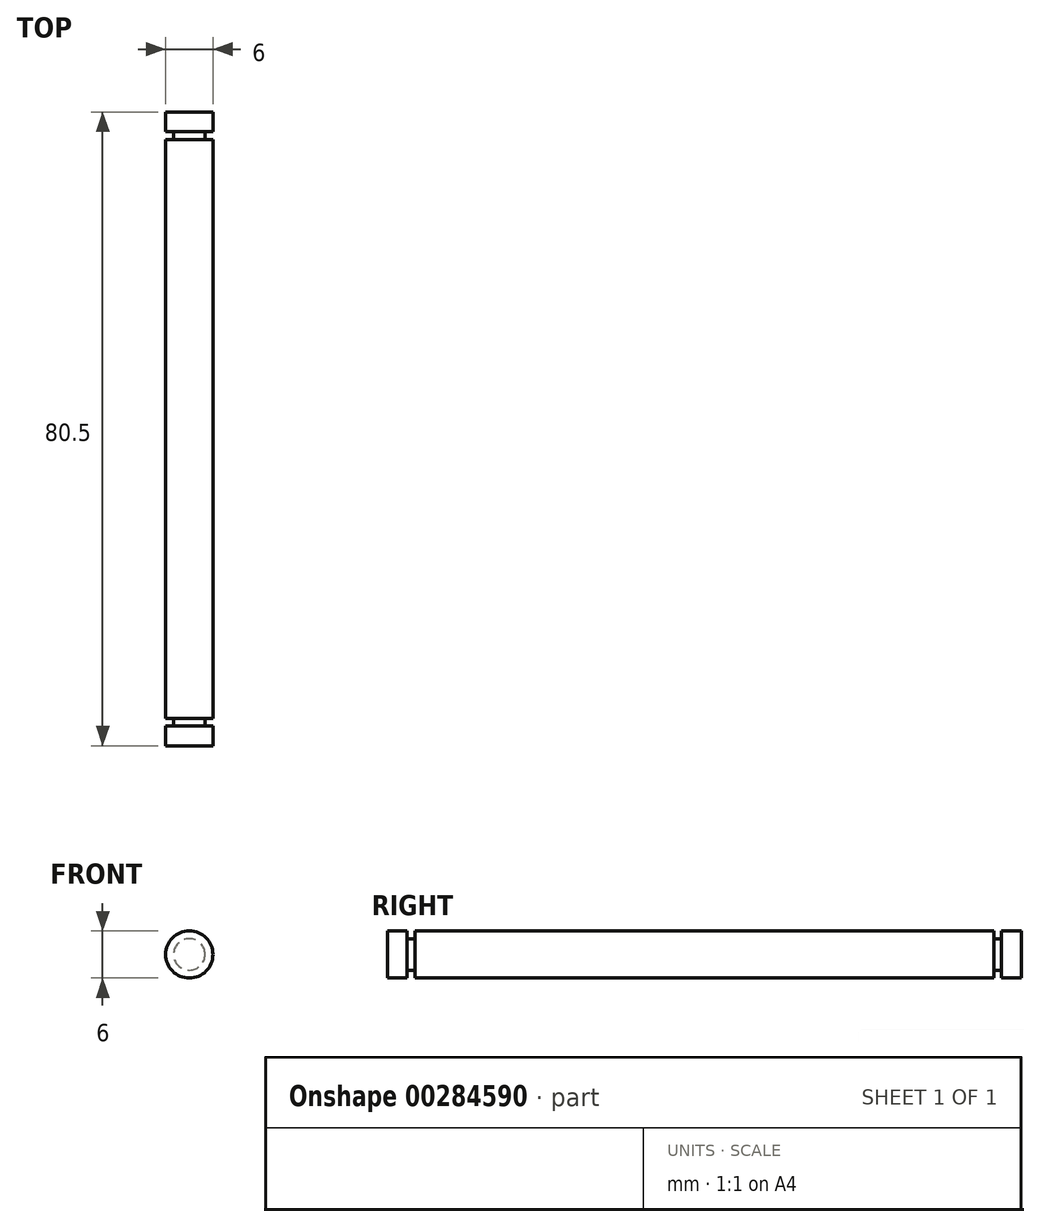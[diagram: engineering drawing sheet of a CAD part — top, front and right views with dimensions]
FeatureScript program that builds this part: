
annotation { "Feature Type Name" : "Feature", "Feature Type Description" : "" }
export const myFeature = defineFeature(function(context is Context, id is Id, definition is map)
    precondition{}
    {
        {
            var Q0;
            Q0=qCreatedBy(makeId("Right.planeOp"),FACE);
            var sketch = newSketch(context, id + "F0", { "sketchPlane" : qUnion([Q0])});
            skLineSegment(sketch, "E0.bottom", {"start": v(0, 0) * mm, "end": v(80.5, 0) * mm});
            skLineSegment(sketch, "E0.top", {"start": v(0, 3) * mm, "end": v(2.5, 3) * mm});
            skLineSegment(sketch, "E0.left", {"start": v(0, 0) * mm, "end": v(0, 3) * mm});
            skLineSegment(sketch, "E0.right", {"start": v(80.5, 0) * mm, "end": v(80.5, 3) * mm});
            skLineSegment(sketch, "E1.top", {"start": v(2.5, 2) * mm, "end": v(3.5, 2) * mm});
            skLineSegment(sketch, "E1.left", {"start": v(2.5, 3) * mm, "end": v(2.5, 2) * mm});
            skLineSegment(sketch, "E1.right", {"start": v(3.5, 3) * mm, "end": v(3.5, 2) * mm});
            skLineSegment(sketch, "E2.top", {"start": v(77, 2) * mm, "end": v(78, 2) * mm});
            skLineSegment(sketch, "E2.left", {"start": v(77, 3) * mm, "end": v(77, 2) * mm});
            skLineSegment(sketch, "E2.right", {"start": v(78, 3) * mm, "end": v(78, 2) * mm});
            skLineSegment(sketch, "E3.trimOffspring", {"start": v(3.5, 3) * mm, "end": v(77, 3) * mm});
            skLineSegment(sketch, "E4.trimOffspring", {"start": v(78, 3) * mm, "end": v(80.5, 3) * mm});
            skSolve(sketch);
        }
        {
            var Q0;
            Q0=qCreatedBy(makeId("Right.planeOp"),FACE);
            var sketch = newSketch(context, id + "F1", { "sketchPlane" : qUnion([Q0])});
            skLineSegment(sketch, "E5", {"start": v(-70.04, 0) * mm, "end": v(106.78, 0) * mm});
            skSolve(sketch);
        }
        {
            var Q0;
            Q0=qSketchRegion(id+"F0",true);
            var Q1;
            Q1=sQuery(id+"F1.wireOp",EDGE,"E5");
            revolve(context, id + "F2", {"entities" : qUnion([Q0]), "axis" : qUnion([Q1]), "revolveType" : RevolveType.FULL});
        }
    });
